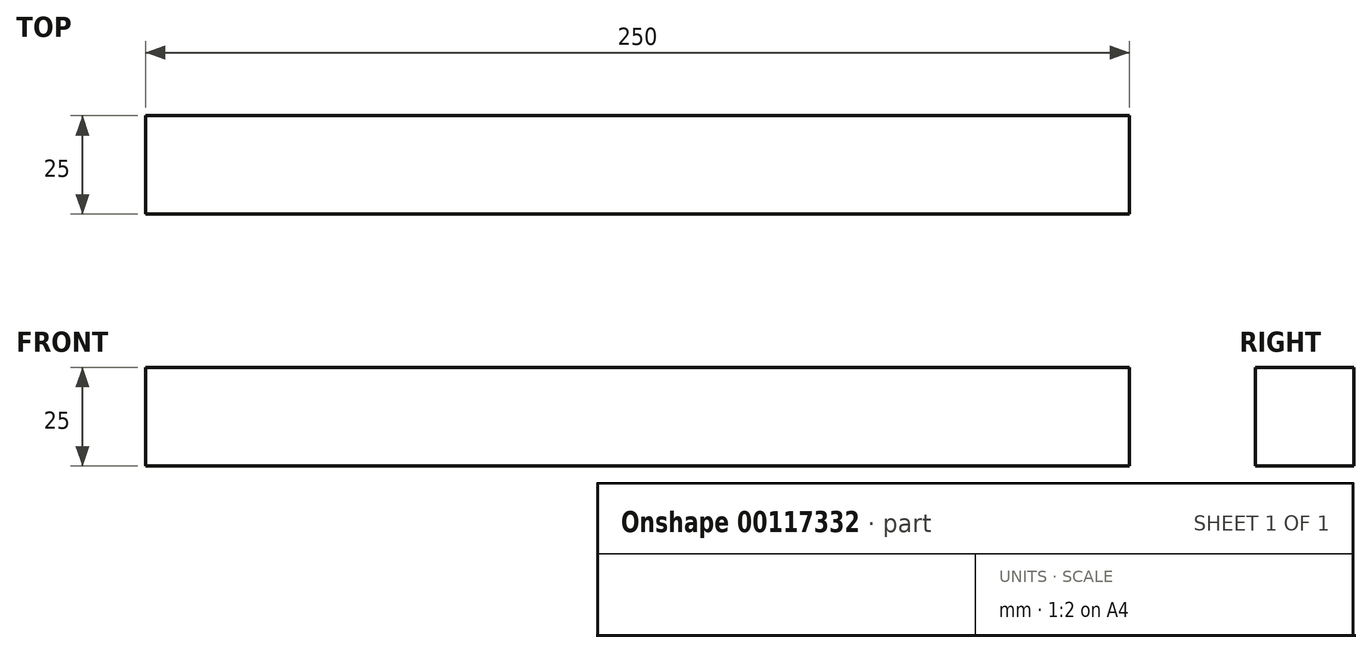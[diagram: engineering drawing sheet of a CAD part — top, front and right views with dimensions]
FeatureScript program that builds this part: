
annotation { "Feature Type Name" : "Feature", "Feature Type Description" : "" }
export const myFeature = defineFeature(function(context is Context, id is Id, definition is map)
    precondition{}
    {
        {
            var Q0;
            Q0=qCreatedBy(makeId("Front.planeOp"),FACE);
            var sketch = newSketch(context, id + "F0", { "sketchPlane" : qUnion([Q0])});
            skLineSegment(sketch, "E0.bottom", {"start": v(0, 0) * mm, "end": v(250, 0) * mm});
            skLineSegment(sketch, "E0.top", {"start": v(0, 25) * mm, "end": v(250, 25) * mm});
            skLineSegment(sketch, "E0.left", {"start": v(0, 0) * mm, "end": v(0, 25) * mm});
            skLineSegment(sketch, "E0.right", {"start": v(250, 0) * mm, "end": v(250, 25) * mm});
            skSolve(sketch);
        }
        {
            var Q0;
            Q0 = qSketchRegion(id + "F0", true);
            extrude(context, id + "F1", {"entities" : qUnion([Q0]), "depth" : 25 * mm});
        }
    });
